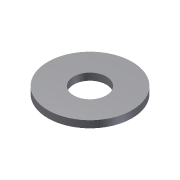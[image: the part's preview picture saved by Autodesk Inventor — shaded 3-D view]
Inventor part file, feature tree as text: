
AUTODESK INVENTOR PART (.ipt)
format: ipt  version: 2012 (Build 160160000, 160)  size: 71,680 bytes
history: native  units: mm
features: extrude x1, sketch x1, reference x1
ambient origin geometry x8: Origin, YZ Plane, XZ Plane, XY Plane, X Axis, Y Axis, Z Axis, Center Point
bodies: Solid1 (feature_tree)
feature tree (3):
  extrude  "Extrusion1"  Depth=3.0mm TaperAngle=0.0deg
  sketch  "Sketch1"  dims[d0=36.0mm d1=3.0mm d2=0.0mm]
  reference  "Reference1"
